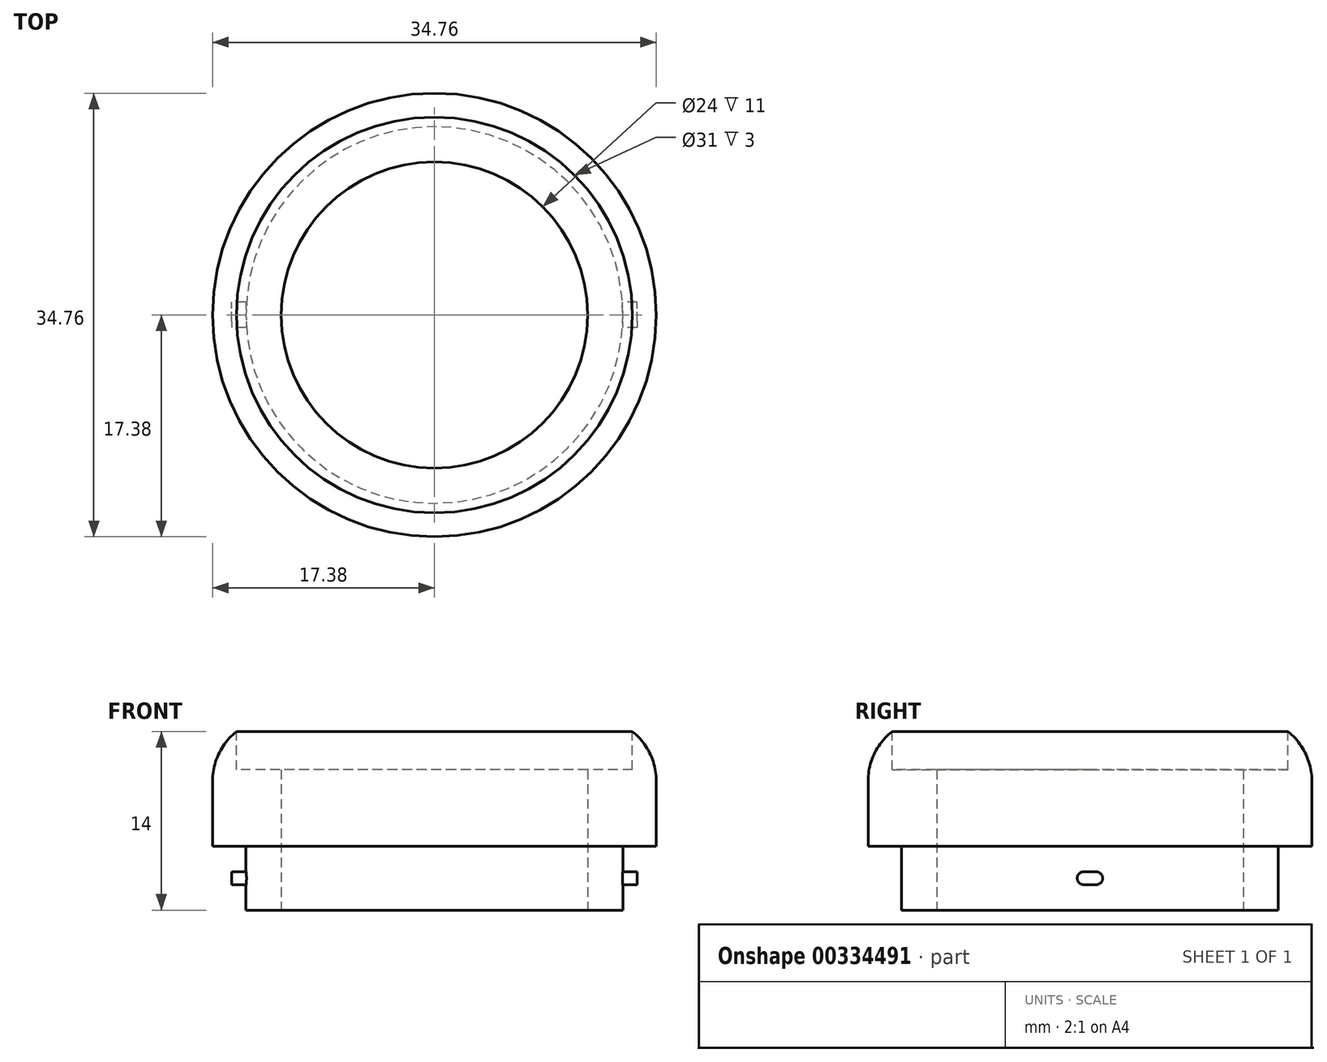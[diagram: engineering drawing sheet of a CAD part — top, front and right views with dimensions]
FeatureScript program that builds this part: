
annotation { "Feature Type Name" : "Feature", "Feature Type Description" : "" }
export const myFeature = defineFeature(function(context is Context, id is Id, definition is map)
    precondition{}
    {
        {
            var Q0;
            Q0=qCreatedBy(makeId("Top.planeOp"),FACE);
            var sketch = newSketch(context, id + "F0", { "sketchPlane" : qUnion([Q0])});
            skCircle(sketch, "E0", {"center": v(0, 0) * mm, "radius": 14.75 * mm});
            skSolve(sketch);
        }
        {
            var Q0;
            Q0=qSketchRegion(id+"F0",true);
            extrude(context, id + "F1", {"entities" : qUnion([Q0]), "depth" : 5 * mm});
        }
        {
            var Q0;
            Q0=makeQuery(id+"F1.opExtrude","CAP_FACE",FACE,{"disambiguationData":[OSD([sQuery(id+"F0.wireOp",EDGE,"E0")])],"isStart":false});
            var sketch = newSketch(context, id + "F2", { "sketchPlane" : qUnion([Q0])});
            skCircle(sketch, "E1", {"center": v(0, 0) * mm, "radius": 17.38 * mm});
            skSolve(sketch);
        }
        {
            var Q0;
            Q0=qSketchRegion(id+"F2",true);
            extrude(context, id + "F3", {"entities" : qUnion([Q0]), "operationType" : NewBodyOperationType.ADD, "depth" : 9 * mm});
        }
        {
            var Q0;
            Q0=qCreatedBy(makeId("Right.planeOp"),FACE);
            var sketch = newSketch(context, id + "F4", { "sketchPlane" : qUnion([Q0])});
            skPoint(sketch, "E2.endSnap0", {"position": v(0, 2.5) * mm});
            skArc(sketch, "E3", {"start": v(-0.5, 3) * mm, "mid": v(-1, 2.5) * mm, "end": v(-0.5, 2) * mm});
            skArc(sketch, "E4.MirrorC", {"start": v(0.5, 3) * mm, "mid": v(1, 2.5) * mm, "end": v(0.5, 2) * mm});
            skLineSegment(sketch, "E5.0", {"start": v(-0.5, 2) * mm, "end": v(0.5, 2) * mm});
            skLineSegment(sketch, "E6.0", {"start": v(-0.5, 3) * mm, "end": v(0.5, 3) * mm});
            skSolve(sketch);
        }
        {
            var Q0;
            Q0=qSketchRegion(id+"F4",true);
            extrude(context, id + "F5", {"entities" : qUnion([Q0]), "operationType" : NewBodyOperationType.ADD, "depth" : 31.75 * mm, "symmetric" : true});
        }
        {
            var Q0;
            Q0=makeQuery(id+"F1.opExtrude","CAP_FACE",FACE,{"disambiguationData":[OSD([sQuery(id+"F0.wireOp",EDGE,"E0")])],"isStart":true});
            var sketch = newSketch(context, id + "F6", { "sketchPlane" : qUnion([Q0])});
            skCircle(sketch, "E7", {"center": v(0, 0) * mm, "radius": 12 * mm});
            skSolve(sketch);
        }
        {
            var Q0;
            Q0=qSketchRegion(id+"F6",true);
            extrude(context, id + "F7", {"entities" : qUnion([Q0]), "operationType" : NewBodyOperationType.REMOVE, "oppositeDirection" : true, "depth" : 15 * mm});
        }
        {
            var Q0;
            Q0=makeQuery(id+"F3.opExtrude","CAP_FACE",FACE,{"disambiguationData":[OSD([sQuery(id+"F2.wireOp",EDGE,"E1")])],"isStart":false});
            var sketch = newSketch(context, id + "F8", { "sketchPlane" : qUnion([Q0])});
            skCircle(sketch, "E8", {"center": v(0, 0) * mm, "radius": 15.5 * mm});
            skSolve(sketch);
        }
        {
            var Q0;
            Q0=qSketchRegion(id+"F8",true);
            extrude(context, id + "F9", {"entities" : qUnion([Q0]), "operationType" : NewBodyOperationType.REMOVE, "oppositeDirection" : true, "depth" : 3 * mm});
        }
        {
            var Q0;
            Q0=makeQuery(id+"F3.opExtrude","CAP_EDGE",EDGE,{"disambiguationData":[OSD([sQuery(id+"F2.wireOp",EDGE,"E1")])],"isStart":false});
            fillet(context, id + "F10", {"entities" : qUnion([Q0]), "radius" : 5 * mm, "tangentPropagation" : true, "allowEdgeOverflow" : false});
        }
    });
